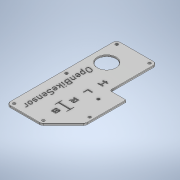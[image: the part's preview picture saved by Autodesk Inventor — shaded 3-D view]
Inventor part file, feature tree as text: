
AUTODESK INVENTOR PART (.ipt)
format: ipt  version: 2020.3 (Build 243373000, 373)  size: 1,042,432 bytes
history: native  units: mm
features: extrude x5, sketch x5, chamfer x1, fillet x1, other x1
ambient origin geometry x8: Origin, YZ Plane, XZ Plane, XY Plane, X Axis, Y Axis, Z Axis, Center Point
bodies: Volumenkörper1 (feature_tree)
feature tree (13):
  extrude  "Extrusion1"  Depth=0.5mm TaperAngle=45.0deg
  chamfer  "Fase1"  Distance=10.0mm
  extrude  "Extrusion2"  Depth=22.0mm
  extrude  "Extrusion3"  Depth=30.0mm
  extrude  "Extrusion4"  Depth=0.5mm
  fillet  "Rundung1"  Radius=0.8mm
  extrude  "Extrusion5"  [1 undecoded]
  sketch  "Skizze1"  dims[d0=10.0mm d1=0.0mm d2=0.5mm d3=125.0mm d4=45.0deg d5=10.0mm d6=0.0mm]
  sketch  "Skizze2"  dims[d7=10.0mm d8=0.0mm d9=22.0mm]
  sketch  "Skizze3"  dims[d10=14.0mm d11=30.0mm]
  sketch  "Skizze4"  dims[d12=10.0mm d13=0.0mm d14=0.5mm d15=0.8mm d16=0.0mm]
  sketch  "Skizze5"
  other  "Körper1"
note: 1 required parameter value undecoded (feature->parameter linkage not recoverable at this tier; creation-order binding heuristic only, values carry confidence <= 0.55)
